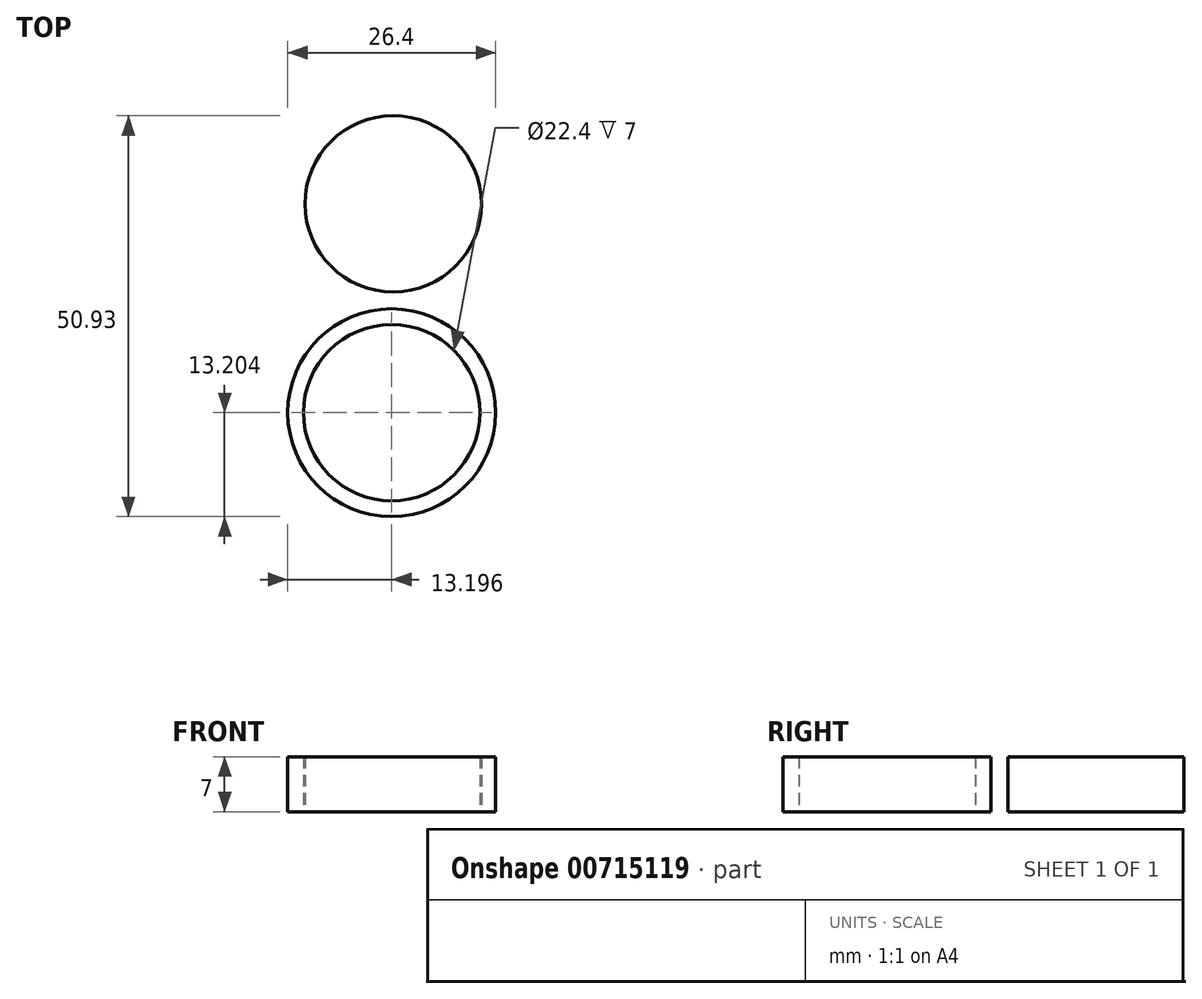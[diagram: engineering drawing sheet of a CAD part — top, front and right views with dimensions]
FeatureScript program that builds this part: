
annotation { "Feature Type Name" : "Feature", "Feature Type Description" : "" }
export const myFeature = defineFeature(function(context is Context, id is Id, definition is map)
    precondition{}
    {
        {
            var Q0;
            Q0=qCreatedBy(makeId("Top.planeOp"),FACE);
            var sketch = newSketch(context, id + "F0", { "sketchPlane" : qUnion([Q0])});
            skCircle(sketch, "E0", {"center": v(0, 0) * mm, "radius": 11.2 * mm});
            skArc(sketch, "E1", {"start": v(-10.33, 8.22) * mm, "mid": v(-13.2, 0.37) * mm, "end": v(-10.77, -7.64) * mm});
            skCircle(sketch, "E2", {"center": v(0, 26.42) * mm, "radius": 11.2 * mm});
            skCircle(sketch, "E3", {"center": v(0, 26.42) * mm, "radius": 13.2 * mm});
            skCircle(sketch, "E4.1.0", {"center": v(-0.2, -26.53) * mm, "radius": 13.2 * mm});
            skCircle(sketch, "E4.1.1", {"center": v(-0.2, -26.53) * mm, "radius": 11.2 * mm});
            skPoint(sketch, "E4.center", {"position": v(-0.1, -0.06) * mm});
            skLineSegment(sketch, "E5", {"start": v(-10.77, -18.62) * mm, "end": v(-10.77, -7.64) * mm});
            skLineSegment(sketch, "E6.1.0", {"start": v(10.77, 18.62) * mm, "end": v(10.77, 7.64) * mm});
            skLineSegment(sketch, "E7", {"start": v(-10.33, 18.2) * mm, "end": v(-10.33, 8.22) * mm});
            skLineSegment(sketch, "E8.1.0", {"start": v(10.33, -18.2) * mm, "end": v(10.33, -8.22) * mm});
            skArc(sketch, "E9.trimOffspring", {"start": v(10.33, -8.22) * mm, "mid": v(13.2, -0.37) * mm, "end": v(10.77, 7.64) * mm});
            skSolve(sketch);
        }
        {
            var Q0;
            Q0=makeQuery(id+"F0.imprint","IMPRINT",FACE,{"disambiguationData":[TD([[makeQuery(id+"F0.imprint","IMPRINT",EDGE,{"derivedFrom":sQuery(id+"F0.wireOp",EDGE,"E4.1.0")}),1.0]])]});
            var Q1;
            Q1=makeQuery(id+"F0.imprint","IMPRINT",FACE,{"disambiguationData":[TD([[makeQuery(id+"F0.imprint","IMPRINT",EDGE,{"derivedFrom":sQuery(id+"F0.wireOp",EDGE,"E0")}),1.0]])]});
            extrude(context, id + "F1", {"entities" : qUnion([Q0, Q1]), "depth" : 7 * mm, "offsetDistance" : 25 * mm});
        }
    });
